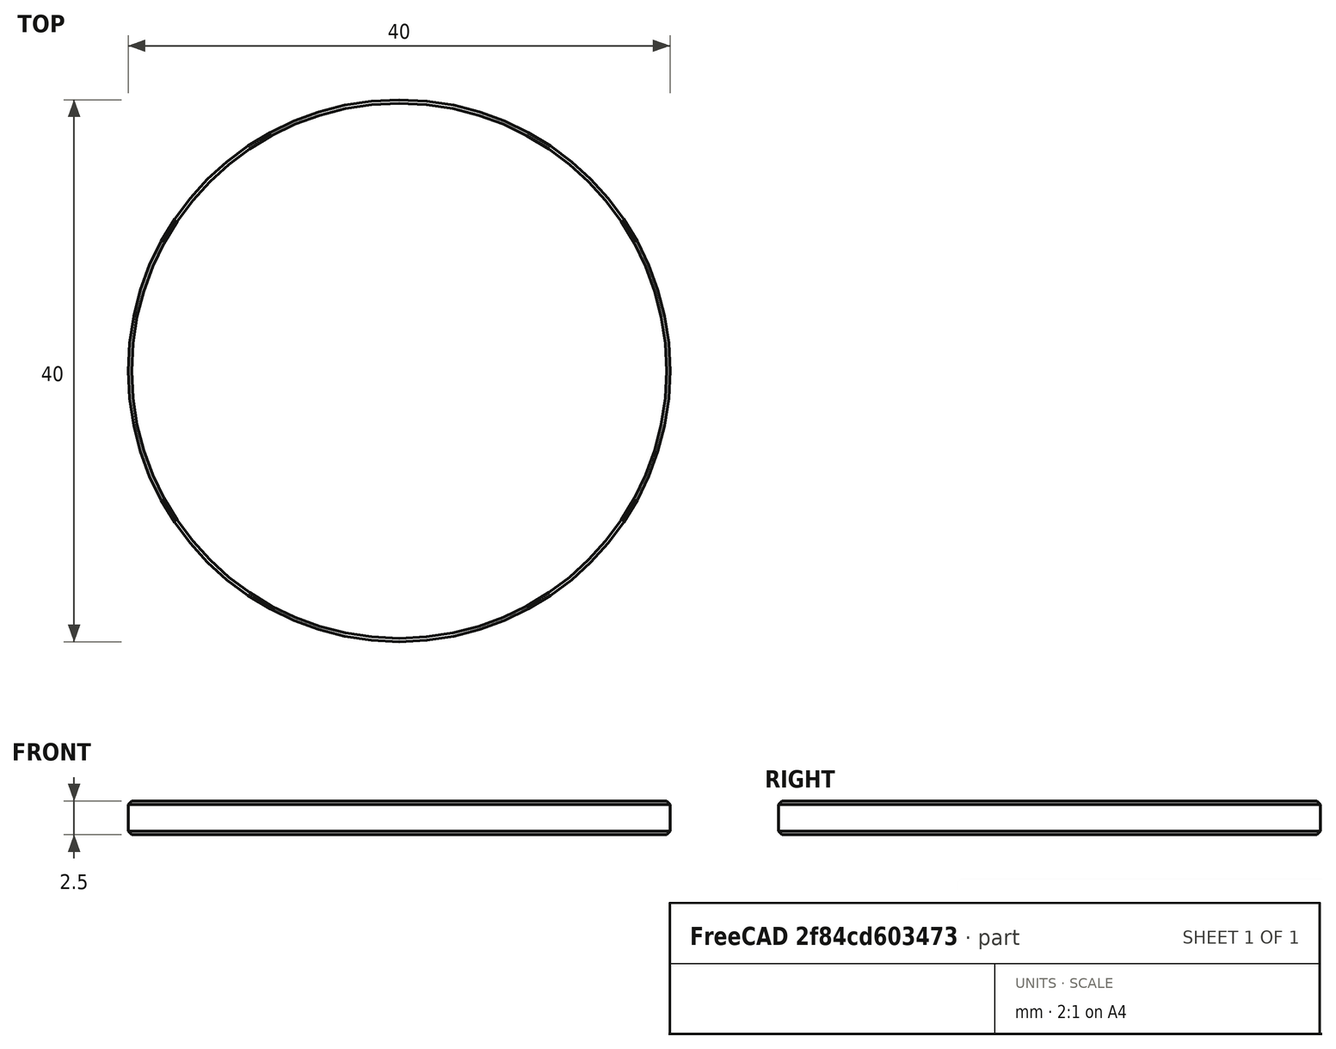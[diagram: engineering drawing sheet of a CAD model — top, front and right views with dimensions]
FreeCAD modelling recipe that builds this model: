
FCSTD DOCUMENT  (FreeCAD 0.20R29603 (Git))
Label: ballerina-coin-71040
License: All rights reserved
LicenseURL: http://en.wikipedia.org/wiki/All_rights_reserved
objects: Sketcher::SketchObject×4, Part::Feature×3, PartDesign::Plane×2, App::DocumentObjectGroup×2, App::TextDocument×1, Spreadsheet::Sheet×1, PartDesign::Revolution×1, PartDesign::Body×1, Part::FeaturePython×1, Mesh::Feature×1
note: 13 computed .brp shape members not serialized (recipe doc carries the construction recipe); baked Part::Feature solids carry a one-line shape summary decoded from their .brp

FEATURE [App::TextDocument] Text_document  label="Text document"
  Text = https://publicdomainvectors.org/en/free-clipart/Vintage-ballerina-silhouette/71040.html
FEATURE [Spreadsheet::Sheet] Spreadsheet
  cells = A2=Vector X center; B2=vec_x; C2(dim_vec_x)==-28 mm; A3=Vector Y center; B3=vec_y; C3(dim_vec_y)==16 mm; A4=Coin radius; B4=coin_r; C4(dim_coin_r)==20 mm; A5=Coin height; B5=coin_h; C5(dim_coin_h)==2.5 mm; D5==2.5 mm; A6=Engrave depth; B6=engrave_h; C6(dim_engrave_h)==dim_coin_h / 2; A7=Chamfer width; B7=chamfer_w; C7(dim_chamfer_w)==dim_coin_h / 10; A8=Chamfer radius; B8=chamfer_r; C8(dim_chamfer_r)==dim_coin_r - dim_chamfer_w; A9=SVG Scale; B9=svg_scale; C9=0.08; A11=Edge dimple radius; B11=dimple_r; C11(dim_dimple_r)==0.5 mm; A12=Edge dimple count; B12=dimple_count; C12(dim_dimple_count)=64
FEATURE [PartDesign::Plane] DatumPlane  label="BaseXYDatumPlane"
  Length = 60
  MapMode = 5
  ResizeMode = 0
  Support = -> [XY_Plane]
  Width = 60
FEATURE [Sketcher::SketchObject] Sketch001  label="CircleSketch"
  FullyConstrained = true
  MapMode = 5
  Support = -> [DatumPlane]
  expr: Constraints[1] = Spreadsheet.dim_coin_r - Spreadsheet.dim_chamfer_w
  expr: Constraints[3] = Spreadsheet.dim_coin_r - 1 mm
  sketch-geometry (6):
    g0: Circle CenterX=0 CenterY=0 CenterZ=0 NormalX=0 NormalY=0 NormalZ=1 AngleXU=0 Radius=19.75
    g1: Circle CenterX=0 CenterY=0 CenterZ=0 NormalX=0 NormalY=0 NormalZ=1 AngleXU=0 Radius=19
    g2: LineSegment StartX=0 StartY=0 StartZ=0 EndX=0 EndY=19 EndZ=0
    g3: LineSegment StartX=0 StartY=0 StartZ=0 EndX=0 EndY=-19 EndZ=0
    g4: LineSegment StartX=0 StartY=0 StartZ=0 EndX=-19 EndY=0 EndZ=0
    g5: LineSegment StartX=0 StartY=0 StartZ=0 EndX=19 EndY=0 EndZ=0
  constraints (16):
    c: Coincident(g0,g-1)
    c: Radius(g0) = 19.75
    c: Coincident(g1,g0)
    c: Radius(g1) = 19
    c: Coincident(g2,g0)
    c: PointOnObject(g2,g1)
    c: Vertical(g2)
    c: Coincident(g3,g0)
    c: PointOnObject(g3,g1)
    c: Vertical(g3)
    c: Coincident(g4,g0)
    c: PointOnObject(g4,g1)
    c: Horizontal(g4)
    c: Coincident(g5,g0)
    c: PointOnObject(g5,g1)
    c: Horizontal(g5)
FEATURE [PartDesign::Plane] DatumPlane001  label="ProfileYZDatumPlane"
  Length = 60
  MapMode = 5
  Placement = pos=(0,0,0) rot=(0.57735,0.57735,0.57735;2.0944rad)
  ResizeMode = 0
  Support = -> [YZ_Plane]
  Width = 60
FEATURE [Sketcher::SketchObject] Sketch  label="CoinProfileSketch"
  FullyConstrained = true
  MapMode = 5
  Placement = pos=(0,0,0) rot=(0.57735,0.57735,0.57735;2.0944rad)
  Support = -> [DatumPlane001]
  expr: Constraints[10] = Spreadsheet.dim_chamfer_w
  expr: Constraints[12] = Spreadsheet.dim_coin_h
  expr: Constraints[13] = Spreadsheet.dim_coin_r
  expr: Constraints[14] = Spreadsheet.dim_coin_r
  expr: Constraints[15] = Spreadsheet.dim_coin_h
  expr: Constraints[16] = Spreadsheet.dim_chamfer_r
  sketch-geometry (11):
    g0: LineSegment StartX=0 StartY=0 StartZ=0 EndX=0 EndY=-2.5 EndZ=0
    g1: LineSegment StartX=19.75 StartY=0 StartZ=0 EndX=20 EndY=-0.25 EndZ=0
    g2: LineSegment StartX=20 StartY=-0.25 StartZ=0 EndX=20 EndY=-2.25 EndZ=0
    g3: LineSegment StartX=20.25 StartY=0 StartZ=0 EndX=20 EndY=0 EndZ=0
    g4: LineSegment StartX=20 StartY=0 StartZ=0 EndX=20 EndY=-0.25 EndZ=0
    g5: LineSegment StartX=20 StartY=-2.25 StartZ=0 EndX=20 EndY=-2.5 EndZ=0
    g6: LineSegment StartX=0 StartY=0 StartZ=0 EndX=19.75 EndY=0 EndZ=0
    g7: LineSegment StartX=19.75 StartY=0 StartZ=0 EndX=20 EndY=0 EndZ=0
    g8: LineSegment StartX=20 StartY=-2.5 StartZ=0 EndX=19.75 EndY=-2.5 EndZ=0
    g9: LineSegment StartX=19.75 StartY=-2.5 StartZ=0 EndX=0 EndY=-2.5 EndZ=0
    g10: LineSegment StartX=19.75 StartY=-2.5 StartZ=0 EndX=20 EndY=-2.25 EndZ=0
  constraints (31):
    c: Vertical(g0)
    c: Coincident(g1,g2)
    c: Vertical(g2)
    c: Horizontal(g3)
    c: Coincident(g4,g3)
    c: Coincident(g4,g1)
    c: Coincident(g5,g2)
    c: Vertical(g5)
    c: Vertical(g4)
    c: Equal(g3,g4)
    c: DistanceY(g5,g5) = 0.25
    c: Equal(g5,g4)
    c: DistanceY(g5,g3) = 2.5
    c: DistanceX(g0,g5) = 20
    c: DistanceX(g-1,g3) = 20
    c: DistanceY(g0,g-1) = 2.5
    c: DistanceX(g1) = 19.75
    c: Coincident(g6,g0)
    c: Coincident(g6,g1)
    c: Horizontal(g6)
    c: Coincident(g7,g1)
    c: Coincident(g7,g3)
    c: Horizontal(g7)
    c: Coincident(g8,g5)
    c: Horizontal(g8)
    c: Coincident(g9,g8)
    c: Coincident(g9,g0)
    c: Horizontal(g9)
    c: Coincident(g10,g9)
    c: Coincident(g10,g2)
    c: Equal(g9,g6)
FEATURE [PartDesign::Revolution] Revolution  label="CoinRevolution"
  Angle = 360
  Axis = (-1e-16,1e-16,1)
  Base = (0,0,0)
  Placement = pos=(0,0,0) rot=(0.57735,0.57735,0.57735;2.0944rad)
  Profile = -> Sketch
  ReferenceAxis = -> Sketch [V_Axis]
  Reversed = true
FEATURE [Sketcher::SketchObject] Sketch002  label="CoinEdgeProfileSketch"
  FullyConstrained = true
  MapMode = 5
  Placement = pos=(0,0,0) rot=(0.57735,0.57735,0.57735;2.0944rad)
  Support = -> [DatumPlane001]
  expr: Constraints[10] = Spreadsheet.dim_coin_r
  expr: Constraints[11] = Spreadsheet.dim_coin_h
  expr: Constraints[17] = Spreadsheet.dim_chamfer_r
  expr: Constraints[6] = Spreadsheet.dim_chamfer_w
  expr: Constraints[8] = Spreadsheet.dim_coin_h
  expr: Constraints[9] = Spreadsheet.dim_coin_r
  sketch-geometry (13):
    g0: LineSegment StartX=0 StartY=2e-16 StartZ=0 EndX=0 EndY=-2.5 EndZ=0
    g1: LineSegment StartX=20 StartY=-0.25 StartZ=0 EndX=20 EndY=-2.25 EndZ=0
    g2: LineSegment StartX=20 StartY=2e-16 StartZ=0 EndX=20 EndY=-0.25 EndZ=0
    g3: LineSegment StartX=20 StartY=-2.25 StartZ=0 EndX=20 EndY=-2.5 EndZ=0
    g4: LineSegment StartX=0 StartY=2e-16 StartZ=0 EndX=19 EndY=2e-16 EndZ=0
    g5: LineSegment StartX=19 StartY=2e-16 StartZ=0 EndX=19 EndY=-2.5 EndZ=0
    g6: LineSegment StartX=19 StartY=2e-16 StartZ=0 EndX=19.75 EndY=2e-16 EndZ=0
    g7: LineSegment StartX=19.75 StartY=2e-16 StartZ=0 EndX=20 EndY=-0.25 EndZ=0
    g8: LineSegment StartX=19.75 StartY=2e-16 StartZ=0 EndX=20 EndY=2e-16 EndZ=0
    g9: LineSegment StartX=20 StartY=-2.5 StartZ=0 EndX=19.75 EndY=-2.5 EndZ=0
    g10: LineSegment StartX=19 StartY=-2.5 StartZ=0 EndX=0 EndY=-2.5 EndZ=0
    g11: LineSegment StartX=19.75 StartY=-2.5 StartZ=0 EndX=20 EndY=-2.25 EndZ=0
    g12: LineSegment StartX=19.75 StartY=-2.5 StartZ=0 EndX=19 EndY=-2.5 EndZ=0
  constraints (36):
    c: Vertical(g0)
    c: Coincident(g0,g4)
    c: Vertical(g1)
    c: Coincident(g3,g1)
    c: Vertical(g3)
    c: Vertical(g2)
    c: DistanceY(g3,g3) = 0.25
    c: Equal(g3,g2)
    c: DistanceY(g3,g2) = 2.5
    c: DistanceX(g0,g3) = 20
    c: DistanceX(g-1,g2) = 20
    c: DistanceY(g0,g-1) = 2.5
    c: Horizontal(g4)
    c: Vertical(g5)
    c: DistanceX(g4,g2) = 1
    c: Coincident(g6,g5)
    c: Horizontal(g6)
    c: DistanceX(g0,g6) = 19.75
    c: Coincident(g7,g6)
    c: Coincident(g7,g1)
    c: Coincident(g8,g6)
    c: Coincident(g8,g2)
    c: Horizontal(g8)
    c: Coincident(g4,g5)
    c: Coincident(g2,g1)
    c: Coincident(g9,g3)
    c: Horizontal(g9)
    c: Coincident(g10,g5)
    c: Coincident(g10,g0)
    c: Horizontal(g10)
    c: Coincident(g11,g9)
    c: Coincident(g11,g1)
    c: Coincident(g12,g11)
    c: Coincident(g12,g5)
    c: Horizontal(g12)
    c: Equal(g12,g6)
FEATURE [Sketcher::SketchObject] Sketch004  label="EdgeDimpleSketch"
  FullyConstrained = true
  MapMode = 5
  Support = -> [DatumPlane]
  expr: Constraints[2] = Spreadsheet.dim_coin_r
  sketch-geometry (2):
    g0: LineSegment StartX=0 StartY=0 StartZ=0 EndX=20 EndY=0 EndZ=0
    g1: Circle CenterX=20 CenterY=0 CenterZ=0 NormalX=0 NormalY=0 NormalZ=1 AngleXU=0 Radius=0.5
  constraints (5):
    c: Horizontal(g0)
    c: Coincident(g1,g0)
    c: DistanceX(g0,g0) = 20
    c: Coincident(g0,g-1)
    c: Radius(g1) = 0.5
FEATURE [PartDesign::Body] Body
  Group = -> [DatumPlane,Sketch001,DatumPlane001,Sketch,Revolution,Sketch002,Sketch004]
  Origin = -> Origin
  Tip = -> Revolution
FEATURE [Part::Feature] path2
  shape: bbox 174.8 x 420 x 2e-07 mm, 0 faces, 0 solids (baked)
FEATURE [Part::Feature] path4
  shape: bbox 0.1511 x 0.1505 x 2e-07 mm, 0 faces, 0 solids (baked)
FEATURE [Part::Feature] path6
  shape: bbox 0.1569 x 0.1511 x 2e-07 mm, 0 faces, 0 solids (baked)
FEATURE [App::DocumentObjectGroup] Group007  label="VectorGroup"
  Group = -> [path2,path4,path6]
FEATURE [Part::FeaturePython] Clone  label="Resize008"  # Draft clone (typed FeaturePython)
  AttacherType = Attacher::AttachEngine3D
  Fuse = false
  Objects = -> [path2,path4,path6]
  Placement = pos=(-28,16,0) rot=(0,0,1;0rad)
  Scale = (0.08,0.08,0.08)
FEATURE [App::DocumentObjectGroup] Group008  label="ResizeGroup"
  Group = -> [Clone]
FEATURE [Mesh::Feature] Mesh  label="Body (Meshed)"
